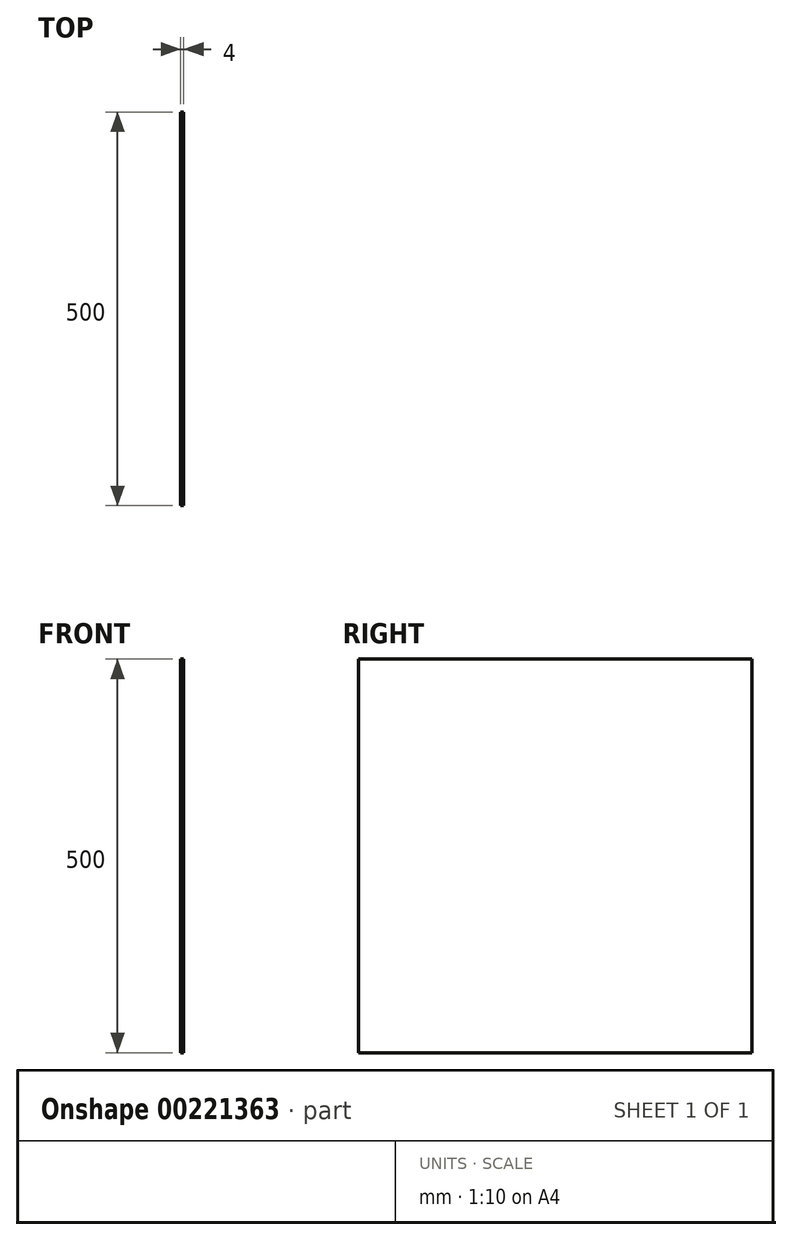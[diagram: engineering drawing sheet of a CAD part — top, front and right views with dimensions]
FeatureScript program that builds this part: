
annotation { "Feature Type Name" : "Feature", "Feature Type Description" : "" }
export const myFeature = defineFeature(function(context is Context, id is Id, definition is map)
    precondition{}
    {
        {
            var Q0;
            Q0=qCreatedBy(makeId("Right.planeOp"),FACE);
            var sketch = newSketch(context, id + "F0", { "sketchPlane" : qUnion([Q0])});
            skLineSegment(sketch, "E0.bottom", {"start": v(250, -250) * mm, "end": v(-250, -250) * mm});
            skLineSegment(sketch, "E0.top", {"start": v(250, 250) * mm, "end": v(-250, 250) * mm});
            skLineSegment(sketch, "E0.left", {"start": v(250, -250) * mm, "end": v(250, 250) * mm});
            skLineSegment(sketch, "E0.right", {"start": v(-250, -250) * mm, "end": v(-250, 250) * mm});
            skPoint(sketch, "E0.middle", {"position": v(0, 0) * mm});
            skSolve(sketch);
        }
        {
            var Q0;
            Q0 = qSketchRegion(id + "F0", true);
            extrude(context, id + "F1", {"entities" : qUnion([Q0]), "depth" : 4 * mm});
        }
    });
